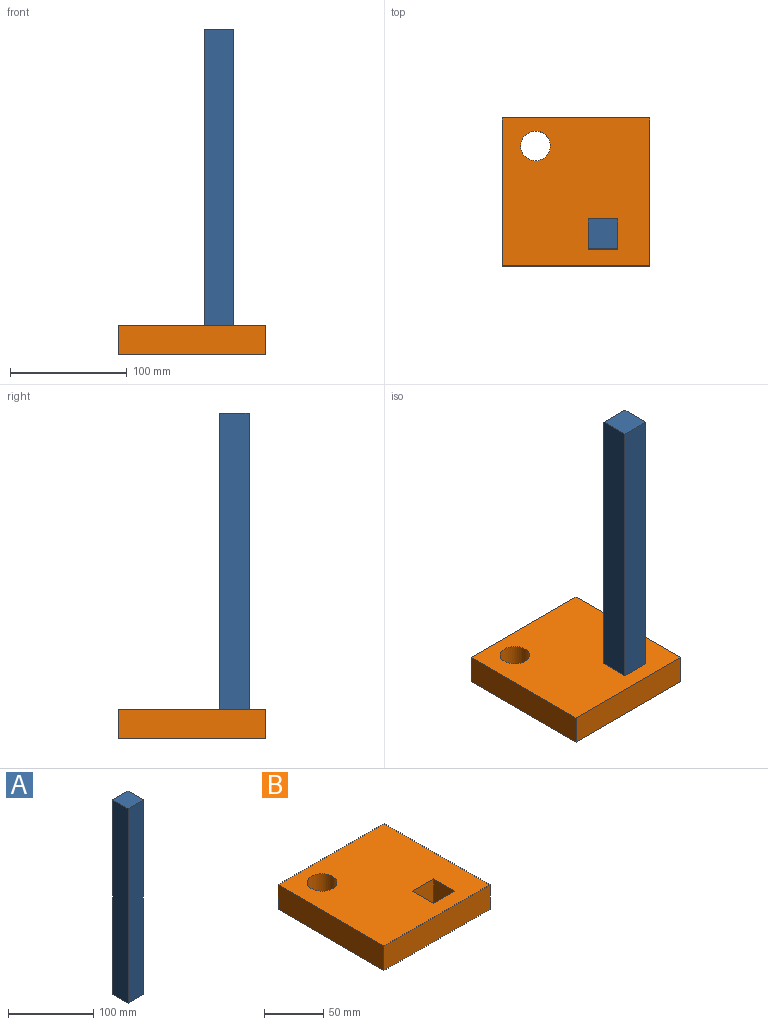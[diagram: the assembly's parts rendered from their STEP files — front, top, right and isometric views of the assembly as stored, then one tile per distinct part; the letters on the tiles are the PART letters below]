
ASSEMBLY  parts=2 mates=1
PART A: 6 faces, bbox 25.4x25.4x279.4 mm
  f0: plane 279.4x25.4mm, normal (-1,0,0), area 7096.8mm2, adj f1,f3,f4,f5
  f1: plane 279.4x25.4mm, normal (0,-1,0), area 7096.8mm2, adj f0,f2,f4,f5
  f2: plane 279.4x25.4mm, normal (1,0,0), area 7096.8mm2, adj f1,f3,f4,f5
  f3: plane 279.4x25.4mm, normal (0,1,0), area 7096.8mm2, adj f0,f2,f4,f5
  f4: plane 25.4x25.4mm, normal (0,0,-1), area 645.2mm2, adj f0,f1,f2,f3
  f5: plane 25.4x25.4mm, normal (0,0,1), area 645.2mm2, adj f0,f1,f2,f3
PART B: 11 faces, bbox 127x127x25.4 mm
  f0: plane 127x25.4mm, normal (-1,0,0), area 3225.8mm2, adj f1,f8,f9,f10
  f1: plane 127x25.4mm, normal (0,-1,0), area 3225.8mm2, adj f0,f2,f9,f10
  f2: plane 127x25.4mm, normal (1,0,0), area 3225.8mm2, adj f1,f8,f9,f10
  f3: plane 25.4x25.4mm, normal (0,1,0), area 645.2mm2, adj f4,f6,f9,f10
  f4: plane 25.4x25.4mm, normal (1,0,0), area 645.2mm2, adj f3,f5,f9,f10
  f5: plane 25.4x25.4mm, normal (0,-1,0), area 645.2mm2, adj f4,f6,f9,f10
  f6: plane 25.4x25.4mm, normal (-1,0,0), area 645.2mm2, adj f3,f5,f9,f10
  f7: cylinder r=12.7mm len=25.4mm, axis (0,0,-1), area 2026.8mm2, adj f9,f10
  f8: plane 127x25.4mm, normal (0,1,0), area 3225.8mm2, adj f0,f2,f9,f10
  f9: plane 127x127mm, normal (0,0,1), area 14977.1mm2, adj f0,f1,f2,f3,f4,f5,f6,f7
  f10: plane 127x127mm, normal (0,0,-1), area 14977.1mm2, adj f0,f1,f2,f3,f4,f5,f6,f7
PLACE A rot(axis=(0,0,-1),90deg) t=(-23.7,81.16,0)mm
PLACE B at identity fixed
MATE slider B.f9 <-> A.f4  axis (0,0,1) through (23.08,-48.99,25.4)mm
